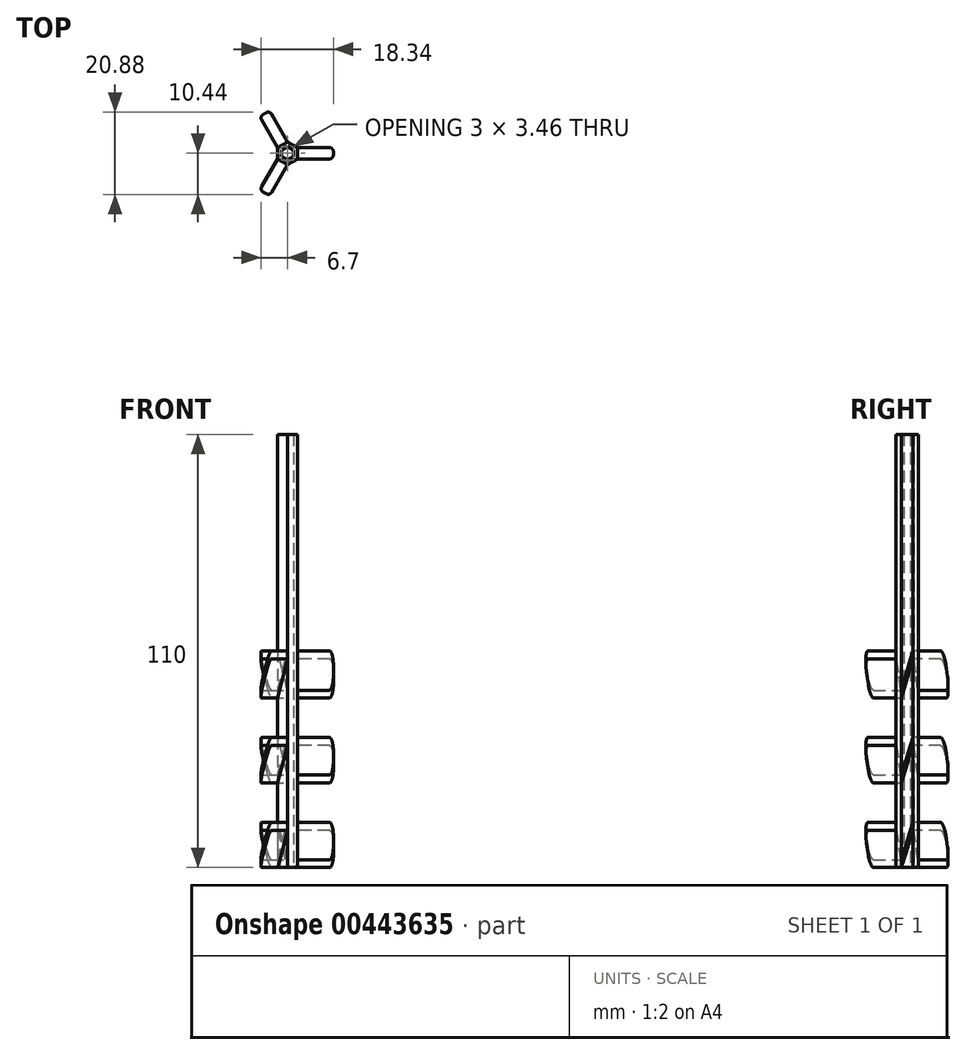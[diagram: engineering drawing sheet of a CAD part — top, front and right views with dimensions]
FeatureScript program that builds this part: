
annotation { "Feature Type Name" : "Feature", "Feature Type Description" : "" }
export const myFeature = defineFeature(function(context is Context, id is Id, definition is map)
    precondition{}
    {
        {
            var Q0;
            Q0=qCreatedBy(makeId("Top.planeOp"),FACE);
            var sketch = newSketch(context, id + "F0", { "sketchPlane" : qUnion([Q0])});
            skCircle(sketch, "E0.cCircle", {"center": v(0, 0) * mm, "radius": 2.5 * mm, "construction": true});
            skLineSegment(sketch, "E0.0", {"start": v(0, 2.89) * mm, "end": v(2.5, 1.44) * mm});
            skLineSegment(sketch, "E0.1", {"start": v(2.5, 1.44) * mm, "end": v(2.5, -1.44) * mm});
            skLineSegment(sketch, "E0.2", {"start": v(2.5, -1.44) * mm, "end": v(0, -2.89) * mm});
            skLineSegment(sketch, "E0.3", {"start": v(0, -2.89) * mm, "end": v(-2.5, -1.44) * mm});
            skLineSegment(sketch, "E0.4", {"start": v(-2.5, -1.44) * mm, "end": v(-2.5, 1.44) * mm});
            skLineSegment(sketch, "E0.5", {"start": v(-2.5, 1.44) * mm, "end": v(0, 2.89) * mm});
            skPoint(sketch, "E0.0.midPoint", {"position": v(1.25, 2.17) * mm});
            skCircle(sketch, "E1.cCircle", {"center": v(0, 0) * mm, "radius": 1.5 * mm, "construction": true});
            skLineSegment(sketch, "E1.0", {"start": v(0, 1.73) * mm, "end": v(1.5, 0.87) * mm});
            skLineSegment(sketch, "E1.1", {"start": v(1.5, 0.87) * mm, "end": v(1.5, -0.87) * mm});
            skLineSegment(sketch, "E1.2", {"start": v(1.5, -0.87) * mm, "end": v(0, -1.73) * mm});
            skLineSegment(sketch, "E1.3", {"start": v(0, -1.73) * mm, "end": v(-1.5, -0.87) * mm});
            skLineSegment(sketch, "E1.4", {"start": v(-1.5, -0.87) * mm, "end": v(-1.5, 0.87) * mm});
            skLineSegment(sketch, "E1.5", {"start": v(-1.5, 0.87) * mm, "end": v(0, 1.73) * mm});
            skPoint(sketch, "E1.0.midPoint", {"position": v(0.75, 1.3) * mm});
            skLineSegment(sketch, "E2", {"start": v(0, 6.56) * mm, "end": v(0, -5.48) * mm, "construction": true});
            skLineSegment(sketch, "E3", {"start": v(-5.15, 0) * mm, "end": v(4.85, 0) * mm, "construction": true});
            skPoint(sketch, "E3.endSnap0", {"position": v(1.5, 0) * mm});
            skSolve(sketch);
        }
        {
            var Q0;
            Q0=makeQuery(id+"F0.imprint","IMPRINT",FACE,{"disambiguationData":[TD([[makeQuery(id+"F0.imprint","IMPRINT",EDGE,{"derivedFrom":sQuery(id+"F0.wireOp",EDGE,"E0.0")}),-1.0]])]});
            extrude(context, id + "F1", {"entities" : qUnion([Q0]), "depth" : 110 * mm});
        }
        {
            var Q0;
            Q0=makeQuery(id+"F1.opExtrude","SWEPT_FACE",FACE,{"disambiguationData":[OSD([sQuery(id+"F0.wireOp",EDGE,"E0.3")])]});
            var sketch = newSketch(context, id + "F2", { "sketchPlane" : qUnion([Q0])});
            skLineSegment(sketch, "E4", {"start": v(0, 110) * mm, "end": v(0, 0) * mm, "construction": true});
            skLineSegment(sketch, "E5", {"start": v(1.44, 53.02) * mm, "end": v(-1.44, 43.02) * mm});
            skLineSegment(sketch, "E6", {"start": v(-1.44, 43.02) * mm, "end": v(-1.44, 45.02) * mm});
            skLineSegment(sketch, "E7", {"start": v(-1.44, 45.02) * mm, "end": v(1.44, 55.02) * mm});
            skLineSegment(sketch, "E8", {"start": v(1.44, 55.02) * mm, "end": v(1.44, 53.02) * mm});
            skLineSegment(sketch, "E9", {"start": v(1.44, 33.02) * mm, "end": v(1.44, 31.02) * mm});
            skLineSegment(sketch, "E10", {"start": v(1.44, 31.02) * mm, "end": v(-1.44, 21.44) * mm});
            skLineSegment(sketch, "E11", {"start": v(-1.44, 21.44) * mm, "end": v(-1.44, 23.44) * mm});
            skLineSegment(sketch, "E12", {"start": v(-1.44, 23.44) * mm, "end": v(1.44, 33.02) * mm});
            skLineSegment(sketch, "E13", {"start": v(1.44, 11.44) * mm, "end": v(1.44, 9.44) * mm});
            skLineSegment(sketch, "E14", {"start": v(1.44, 9.44) * mm, "end": v(-1.44, -0.13) * mm});
            skLineSegment(sketch, "E15", {"start": v(-1.44, -0.13) * mm, "end": v(-1.44, 1.87) * mm});
            skLineSegment(sketch, "E16", {"start": v(-1.44, 1.87) * mm, "end": v(1.44, 11.44) * mm});
            skSolve(sketch);
        }
        {
            var Q0;
            Q0=makeQuery(id+"F2.imprint","IMPRINT",FACE,{"disambiguationData":[TD([[makeQuery(id+"F2.imprint","IMPRINT",EDGE,{"derivedFrom":sQuery(id+"F2.wireOp",EDGE,"E5")}),-1.0]])]});
            var Q1;
            Q1=makeQuery(id+"F2.imprint","IMPRINT",FACE,{"disambiguationData":[TD([[makeQuery(id+"F2.imprint","IMPRINT",EDGE,{"derivedFrom":sQuery(id+"F2.wireOp",EDGE,"E9")}),-1.0]])]});
            var Q2;
            Q2=makeQuery(id+"F2.imprint","IMPRINT",FACE,{"disambiguationData":[TD([[makeQuery(id+"F2.imprint","IMPRINT",EDGE,{"derivedFrom":sQuery(id+"F2.wireOp",EDGE,"E13")}),-1.0]])]});
            extrude(context, id + "F3", {"entities" : qUnion([Q0, Q1, Q2]), "operationType" : NewBodyOperationType.ADD, "depth" : 9.14 * mm});
        }
        {
            var Q0;
            Q0=makeQuery(id+"F1.opExtrude","SWEPT_FACE",FACE,{"disambiguationData":[OSD([sQuery(id+"F0.wireOp",EDGE,"E0.5")])]});
            var sketch = newSketch(context, id + "F4", { "sketchPlane" : qUnion([Q0])});
            skLineSegment(sketch, "E17", {"start": v(0, 110) * mm, "end": v(0, 0) * mm, "construction": true});
            skLineSegment(sketch, "E18", {"start": v(1.44, 53.02) * mm, "end": v(-1.44, 43.02) * mm});
            skLineSegment(sketch, "E19", {"start": v(-1.44, 43.02) * mm, "end": v(-1.44, 45.02) * mm});
            skLineSegment(sketch, "E20", {"start": v(-1.44, 45.02) * mm, "end": v(1.44, 55.02) * mm});
            skLineSegment(sketch, "E21", {"start": v(1.44, 55.02) * mm, "end": v(1.44, 53.02) * mm});
            skLineSegment(sketch, "E22", {"start": v(1.44, 33.02) * mm, "end": v(1.44, 31.02) * mm});
            skLineSegment(sketch, "E23", {"start": v(1.44, 31.02) * mm, "end": v(-1.44, 21.44) * mm});
            skLineSegment(sketch, "E24", {"start": v(-1.44, 21.44) * mm, "end": v(-1.44, 23.44) * mm});
            skLineSegment(sketch, "E25", {"start": v(-1.44, 23.44) * mm, "end": v(1.44, 33.02) * mm});
            skLineSegment(sketch, "E26", {"start": v(1.44, 11.44) * mm, "end": v(1.44, 9.44) * mm});
            skLineSegment(sketch, "E27", {"start": v(1.44, 9.44) * mm, "end": v(-1.44, -0.13) * mm});
            skLineSegment(sketch, "E28", {"start": v(-1.44, -0.13) * mm, "end": v(-1.44, 1.87) * mm});
            skLineSegment(sketch, "E29", {"start": v(-1.44, 1.87) * mm, "end": v(1.44, 11.44) * mm});
            skSolve(sketch);
        }
        {
            var Q0;
            Q0=makeQuery(id+"F4.imprint","IMPRINT",FACE,{"disambiguationData":[TD([[makeQuery(id+"F4.imprint","IMPRINT",EDGE,{"derivedFrom":sQuery(id+"F4.wireOp",EDGE,"E18")}),-1.0]])]});
            var Q1;
            Q1=makeQuery(id+"F4.imprint","IMPRINT",FACE,{"disambiguationData":[TD([[makeQuery(id+"F4.imprint","IMPRINT",EDGE,{"derivedFrom":sQuery(id+"F4.wireOp",EDGE,"E22")}),-1.0]])]});
            var Q2;
            Q2=makeQuery(id+"F4.imprint","IMPRINT",FACE,{"disambiguationData":[TD([[makeQuery(id+"F4.imprint","IMPRINT",EDGE,{"derivedFrom":sQuery(id+"F4.wireOp",EDGE,"E26")}),-1.0]])]});
            extrude(context, id + "F5", {"entities" : qUnion([Q0, Q1, Q2]), "operationType" : NewBodyOperationType.ADD, "depth" : 9.14 * mm});
        }
        {
            var Q0;
            Q0=makeQuery(id+"F1.opExtrude","SWEPT_FACE",FACE,{"disambiguationData":[OSD([sQuery(id+"F0.wireOp",EDGE,"E0.1")])]});
            var sketch = newSketch(context, id + "F6", { "sketchPlane" : qUnion([Q0])});
            skLineSegment(sketch, "E30", {"start": v(0, 110) * mm, "end": v(0, 0) * mm, "construction": true});
            skLineSegment(sketch, "E31", {"start": v(1.44, 53.02) * mm, "end": v(-1.44, 43.02) * mm});
            skLineSegment(sketch, "E32", {"start": v(-1.44, 43.02) * mm, "end": v(-1.44, 45.02) * mm});
            skLineSegment(sketch, "E33", {"start": v(-1.44, 45.02) * mm, "end": v(1.44, 55.02) * mm});
            skLineSegment(sketch, "E34", {"start": v(1.44, 55.02) * mm, "end": v(1.44, 53.02) * mm});
            skLineSegment(sketch, "E35", {"start": v(1.44, 33.02) * mm, "end": v(1.44, 31.02) * mm});
            skLineSegment(sketch, "E36", {"start": v(1.44, 31.02) * mm, "end": v(-1.44, 21.44) * mm});
            skLineSegment(sketch, "E37", {"start": v(-1.44, 21.44) * mm, "end": v(-1.44, 23.44) * mm});
            skLineSegment(sketch, "E38", {"start": v(-1.44, 23.44) * mm, "end": v(1.44, 33.02) * mm});
            skLineSegment(sketch, "E39", {"start": v(1.44, 11.44) * mm, "end": v(1.44, 9.44) * mm});
            skLineSegment(sketch, "E40", {"start": v(1.44, 9.44) * mm, "end": v(-1.44, -0.13) * mm});
            skLineSegment(sketch, "E41", {"start": v(-1.44, -0.13) * mm, "end": v(-1.44, 1.87) * mm});
            skLineSegment(sketch, "E42", {"start": v(-1.44, 1.87) * mm, "end": v(1.44, 11.44) * mm});
            skSolve(sketch);
        }
        {
            var Q0;
            Q0=makeQuery(id+"F6.imprint","IMPRINT",FACE,{"disambiguationData":[TD([[makeQuery(id+"F6.imprint","IMPRINT",EDGE,{"derivedFrom":sQuery(id+"F6.wireOp",EDGE,"E31")}),-1.0]])]});
            var Q1;
            Q1=makeQuery(id+"F6.imprint","IMPRINT",FACE,{"disambiguationData":[TD([[makeQuery(id+"F6.imprint","IMPRINT",EDGE,{"derivedFrom":sQuery(id+"F6.wireOp",EDGE,"E35")}),-1.0]])]});
            var Q2;
            Q2=makeQuery(id+"F6.imprint","IMPRINT",FACE,{"disambiguationData":[TD([[makeQuery(id+"F6.imprint","IMPRINT",EDGE,{"derivedFrom":sQuery(id+"F6.wireOp",EDGE,"E39")}),-1.0]])]});
            extrude(context, id + "F7", {"entities" : qUnion([Q0, Q1, Q2]), "operationType" : NewBodyOperationType.ADD, "depth" : 9.14 * mm});
        }
        {
            var Q0;
            Q0=makeQuery(id+"F3.opExtrude","CAP_EDGE",EDGE,{"disambiguationData":[OSD([sQuery(id+"F2.wireOp",EDGE,"E6")])],"isStart":false});
            var Q1;
            Q1=makeQuery(id+"F3.opExtrude","CAP_EDGE",EDGE,{"disambiguationData":[OSD([sQuery(id+"F2.wireOp",EDGE,"E8")])],"isStart":false});
            var Q2;
            Q2=makeQuery(id+"F3.opExtrude","CAP_EDGE",EDGE,{"disambiguationData":[OSD([sQuery(id+"F2.wireOp",EDGE,"E9")])],"isStart":false});
            var Q3;
            Q3=makeQuery(id+"F3.opExtrude","CAP_EDGE",EDGE,{"disambiguationData":[OSD([sQuery(id+"F2.wireOp",EDGE,"E11")])],"isStart":false});
            var Q4;
            Q4=makeQuery(id+"F3.opExtrude","CAP_EDGE",EDGE,{"disambiguationData":[OSD([sQuery(id+"F2.wireOp",EDGE,"E13")])],"isStart":false});
            var Q5;
            Q5=makeQuery(id+"F3.opExtrude","CAP_EDGE",EDGE,{"disambiguationData":[OSD([sQuery(id+"F2.wireOp",EDGE,"E15")])],"isStart":false});
            var Q6;
            Q6=makeQuery(id+"F7.opExtrude","CAP_EDGE",EDGE,{"disambiguationData":[OSD([sQuery(id+"F6.wireOp",EDGE,"E34")])],"isStart":false});
            var Q7;
            Q7=makeQuery(id+"F7.opExtrude","CAP_EDGE",EDGE,{"disambiguationData":[OSD([sQuery(id+"F6.wireOp",EDGE,"E32")])],"isStart":false});
            var Q8;
            Q8=makeQuery(id+"F7.opExtrude","CAP_EDGE",EDGE,{"disambiguationData":[OSD([sQuery(id+"F6.wireOp",EDGE,"E35")])],"isStart":false});
            var Q9;
            Q9=makeQuery(id+"F7.opExtrude","CAP_EDGE",EDGE,{"disambiguationData":[OSD([sQuery(id+"F6.wireOp",EDGE,"E37")])],"isStart":false});
            var Q10;
            Q10=makeQuery(id+"F7.opExtrude","CAP_EDGE",EDGE,{"disambiguationData":[OSD([sQuery(id+"F6.wireOp",EDGE,"E39")])],"isStart":false});
            var Q11;
            Q11=makeQuery(id+"F7.opExtrude","CAP_EDGE",EDGE,{"disambiguationData":[OSD([sQuery(id+"F6.wireOp",EDGE,"E41")])],"isStart":false});
            var Q12;
            Q12=makeQuery(id+"F5.opExtrude","CAP_EDGE",EDGE,{"disambiguationData":[OSD([sQuery(id+"F4.wireOp",EDGE,"E21")])],"isStart":false});
            var Q13;
            Q13=makeQuery(id+"F5.opExtrude","CAP_EDGE",EDGE,{"disambiguationData":[OSD([sQuery(id+"F4.wireOp",EDGE,"E22")])],"isStart":false});
            var Q14;
            Q14=makeQuery(id+"F5.opExtrude","CAP_EDGE",EDGE,{"disambiguationData":[OSD([sQuery(id+"F4.wireOp",EDGE,"E26")])],"isStart":false});
            var Q15;
            Q15=makeQuery(id+"F5.opExtrude","CAP_EDGE",EDGE,{"disambiguationData":[OSD([sQuery(id+"F4.wireOp",EDGE,"E24")])],"isStart":false});
            var Q16;
            Q16=makeQuery(id+"F5.opExtrude","CAP_EDGE",EDGE,{"disambiguationData":[OSD([sQuery(id+"F4.wireOp",EDGE,"E28")])],"isStart":false});
            var Q17;
            Q17=makeQuery(id+"F5.opExtrude","CAP_EDGE",EDGE,{"disambiguationData":[OSD([sQuery(id+"F4.wireOp",EDGE,"E19")])],"isStart":false});
            fillet(context, id + "F8", {"entities" : qUnion([Q0, Q1, Q2, Q3, Q4, Q5, Q6, Q7, Q8, Q9, Q10, Q11, Q12, Q13, Q14, Q15, Q16, Q17]), "radius" : 1 * mm, "tangentPropagation" : true, "allowEdgeOverflow" : false});
        }
        {
            var Q0;
            Q0=makeQuery(id+"F1.opExtrude","CAP_EDGE",EDGE,{"disambiguationData":[OSD([sQuery(id+"F0.wireOp",EDGE,"E0.2")])],"isStart":true});
            var Q1;
            Q1=makeQuery(id+"F1.opExtrude","CAP_EDGE",EDGE,{"disambiguationData":[OSD([sQuery(id+"F0.wireOp",EDGE,"E0.3")])],"isStart":true});
            var Q2;
            Q2=makeQuery(id+"F1.opExtrude","CAP_EDGE",EDGE,{"disambiguationData":[OSD([sQuery(id+"F0.wireOp",EDGE,"E0.4")])],"isStart":true});
            var Q3;
            Q3=makeQuery(id+"F1.opExtrude","CAP_EDGE",EDGE,{"disambiguationData":[OSD([sQuery(id+"F0.wireOp",EDGE,"E0.5")])],"isStart":true});
            var Q4;
            Q4=makeQuery(id+"F1.opExtrude","CAP_EDGE",EDGE,{"disambiguationData":[OSD([sQuery(id+"F0.wireOp",EDGE,"E0.0")])],"isStart":true});
            var Q5;
            Q5=makeQuery(id+"F1.opExtrude","CAP_EDGE",EDGE,{"disambiguationData":[OSD([sQuery(id+"F0.wireOp",EDGE,"E0.1")])],"isStart":true});
            fillet(context, id + "F9", {"entities" : qUnion([Q0, Q1, Q2, Q3, Q4, Q5]), "radius" : 0.5 * mm, "tangentPropagation" : true, "allowEdgeOverflow" : false});
        }
    });
